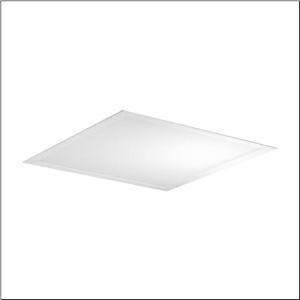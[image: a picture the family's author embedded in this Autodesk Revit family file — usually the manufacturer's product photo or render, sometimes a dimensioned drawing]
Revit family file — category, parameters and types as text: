
# Revit family: apollon_r__21_square_51mq11w72414m_ca44
name_source: partatom
category: Lighting Fixtures
units: mm (PartAtom-declared; Revit-internal decimal feet)

## family parameters
Cut with Voids When Loaded = No
Host = Face
Light Source = No
Part Type = Normal
Room Calculation Point = No
Round Connector Dimension = Use Diameter
Shared = No

## types (1)
- Apollon® 21 square (1 x LED, 4200 lm, 23.3 W, 4000K)
    Apparent Load = 23 VA
    CIE Flux Codes = 60 87 97 100 100
    Color Rendering = 80
    Color Temperature = 4000K
    Default Elevation = 1800 mm
    Description = Apollon® 21 square, office luminaire, primary optical cover: micro prismatic cover, of PMMA, CAT 2 (L<= 3000cd/m²), light emission: direct distribution, primary light characteristic: symmetric, installation type: lay-in mounting, LED, rated luminous flux: 4.200lm, luminous efficacy: 180lm/W, light colour: 840, colour temperature: 4000K, with terminal, 3-pole, mains connection: 220..240V, AC/DC, 0/50..60Hz, rated input power: 23.3W, housing, of aluminium, coated, traffic white (RAL 9016), module: M625, length: 620mm, width: 620mm, height: 30mm, housing upper side, of sheet steel, galvanised, protection rating (complete): IP20, protection rating (lamp compartment, on room side): IP50, insulation class (complete): insulation class II (safety insulation), certification: CE, ENEC, impact resistance: IK03, permissible operating ambient temperature: -20..+45°C, permissible storage temperature: -40..+80°C, packaging unit: set of 5
    Height = 0 mm  [stored 0 ft]
    Lamp = 1 x LED
    Lamp Light Flux = 4200 lm
    Lamp Power = 23.3 W
    Lamp count = 1
    Length = 620 mm
    Luminous efficacy = 180 lm/W
    Manufacturer = Siteco
    ModVariant = No
    Model = 51MQ11W72414M
    Mounting Place = Ceiling
    Mounting Type = Recessed
    Number of Poles = 1
    OnlyDefault = Yes
    Power Factor = 1
    Product Name = Apollon® 21 square
    Product group = office luminaire | ceiling recessed
    ProductGroupID = 401
    Protection Class = Protection class II
    Protection Degree = IP 20
    RLX_Detail_Level = 1
    RLX_Emergency_Light_Flux = 0 lm
    RLX_Emergency_Type = 0
    RLX_Emergency_Type_DB = No
    RlxData = <blob elided: 12977 chars, md5=8199e2ad>
    Socket = socket
    Standby Power = 0 W
    System Light Flux = 4200 lm
    System Power = 23 W
    Type Comments = Product without accessories
    Type Image = l_1291054.jpg
    URL = http://relux.com
    VarID = ---
    Voltage = 0 V
    Weight = 0.00 kg
    Width = 620 mm

note: [stored X ft] marks values corroborated as IEEE doubles in the binary element streams (Revit-internal decimal feet)

## geometry (parser evidence)
native form markers: Sweep x12
no freeform markers — native parametric forms only
